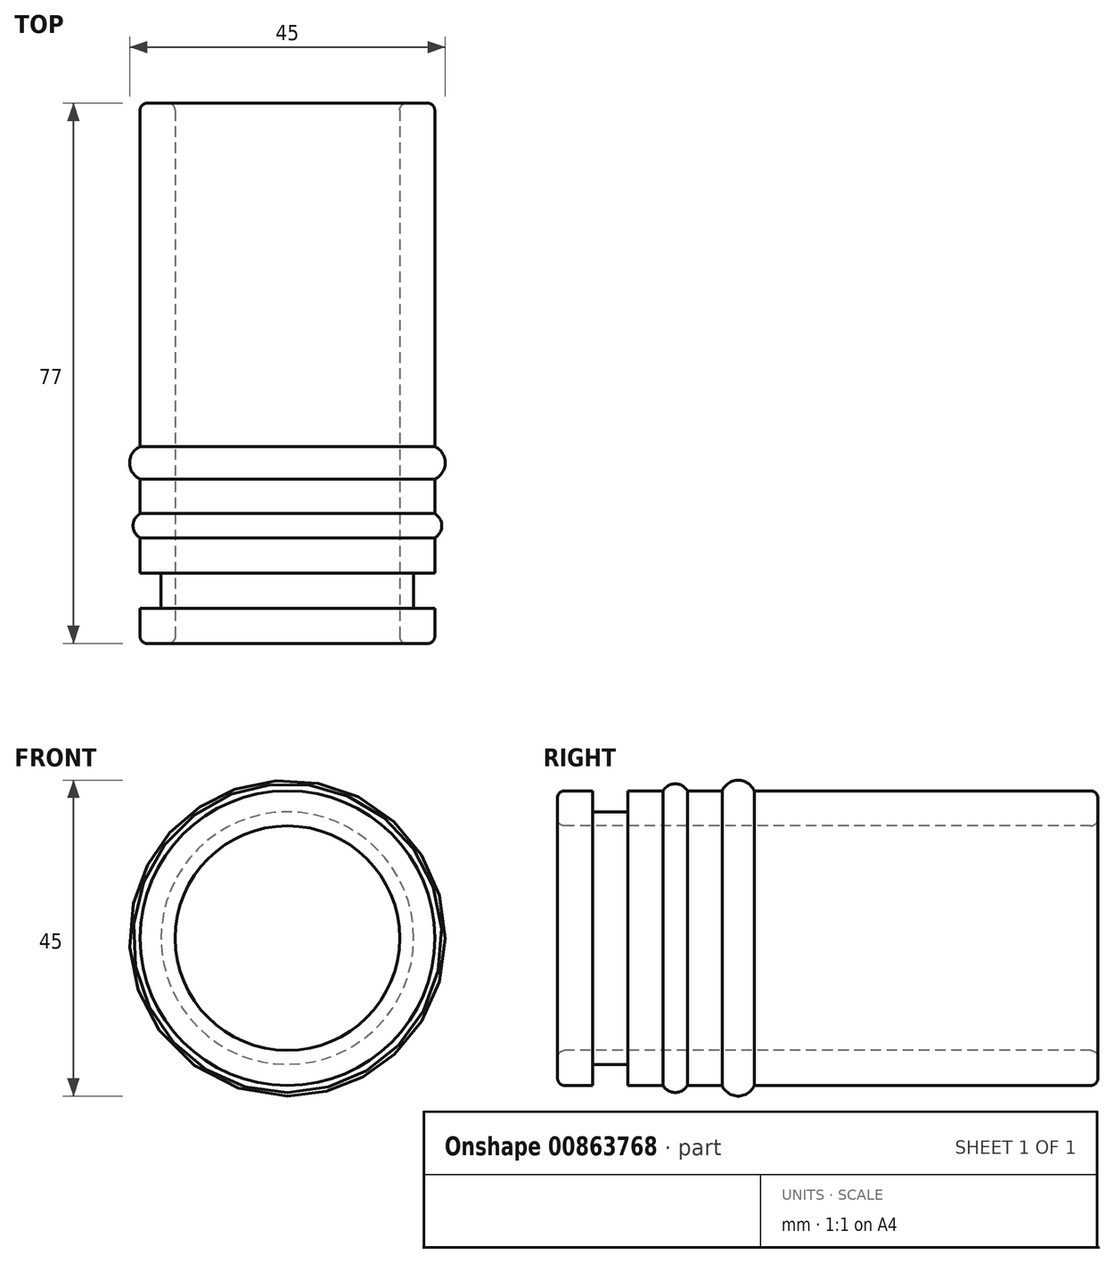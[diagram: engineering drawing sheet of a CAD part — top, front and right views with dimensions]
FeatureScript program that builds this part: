
annotation { "Feature Type Name" : "Feature", "Feature Type Description" : "" }
export const myFeature = defineFeature(function(context is Context, id is Id, definition is map)
    precondition{}
    {
        {
            var Q0;
            Q0=qCreatedBy(makeId("Right.planeOp"),FACE);
            var sketch = newSketch(context, id + "F0", { "sketchPlane" : qUnion([Q0])});
            skLineSegment(sketch, "E0", {"start": v(-27.38, 21) * mm, "end": v(-23.38, 21) * mm});
            skLineSegment(sketch, "E1", {"start": v(48.62, 20) * mm, "end": v(48.62, 17) * mm});
            skLineSegment(sketch, "E2", {"start": v(47.62, 16) * mm, "end": v(-27.38, 16) * mm});
            skLineSegment(sketch, "E3", {"start": v(-28.38, 17) * mm, "end": v(-28.38, 20) * mm});
            skArc(sketch, "E4", {"start": v(-9.87, 21) * mm, "mid": v(-11.6, 22) * mm, "end": v(-13.33, 21) * mm});
            skArc(sketch, "E5", {"start": v(-0.35, 21) * mm, "mid": v(-2.64, 22.5) * mm, "end": v(-4.93, 21) * mm});
            skPoint(sketch, "E6.visualSharp", {"position": v(-28.38, 21) * mm});
            skArc(sketch, "E6.filletArc", {"start": v(-27.38, 21) * mm, "mid": v(-28.08, 20.7) * mm, "end": v(-28.38, 20) * mm});
            skPoint(sketch, "E7.visualSharp", {"position": v(-28.38, 16) * mm});
            skArc(sketch, "E7.filletArc", {"start": v(-28.38, 17) * mm, "mid": v(-28.08, 16.3) * mm, "end": v(-27.38, 16) * mm});
            skPoint(sketch, "E8.visualSharp", {"position": v(48.62, 16) * mm});
            skArc(sketch, "E8.filletArc", {"start": v(47.62, 16) * mm, "mid": v(48.33, 16.3) * mm, "end": v(48.62, 17) * mm});
            skPoint(sketch, "E9.visualSharp", {"position": v(48.62, 21) * mm});
            skArc(sketch, "E9.filletArc", {"start": v(48.62, 20) * mm, "mid": v(48.33, 20.7) * mm, "end": v(47.62, 21) * mm});
            skLineSegment(sketch, "E10.top", {"start": v(-23.38, 18) * mm, "end": v(-18.38, 18) * mm});
            skLineSegment(sketch, "E10.left", {"start": v(-23.38, 21) * mm, "end": v(-23.38, 18) * mm});
            skLineSegment(sketch, "E10.right", {"start": v(-18.38, 21) * mm, "end": v(-18.38, 18) * mm});
            skLineSegment(sketch, "E11.trimOffspring", {"start": v(-18.38, 21) * mm, "end": v(47.62, 21) * mm});
            skLineSegment(sketch, "E12", {"start": v(0, 0) * mm, "end": v(13.85, 0) * mm});
            skSolve(sketch);
        }
        {
            var Q0;
            Q0=makeQuery(id+"F0.imprint","IMPRINT",FACE,{"disambiguationData":[TD([[makeQuery(id+"F0.imprint","IMPRINT",EDGE,{"derivedFrom":sQuery(id+"F0.wireOp",EDGE,"E0")}),-1.0]])]});
            var Q1;
            {var subQ0=sQuery(id+"F0.wireOp",EDGE,"E4");Q1=makeQuery(id+"F0.imprint","IMPRINT",FACE,{"disambiguationData":[TD([[makeQuery(id+"F0.imprint","IMPRINT",EDGE,{"derivedFrom":subQ0}),1.0]])]});}
            var Q2;
            {var subQ0=sQuery(id+"F0.wireOp",EDGE,"E5");Q2=makeQuery(id+"F0.imprint","IMPRINT",FACE,{"disambiguationData":[TD([[makeQuery(id+"F0.imprint","IMPRINT",EDGE,{"derivedFrom":subQ0}),1.0]])]});}
            var Q3;
            Q3=sQuery(id+"F0.wireOp",EDGE,"E12");
            revolve(context, id + "F1", {"surfaceOperationType" : NewSurfaceOperationType.NEW, "entities" : qUnion([Q0, Q1, Q2]), "axis" : qUnion([Q3]), "revolveType" : RevolveType.FULL});
        }
    });
